# Revit family: CUSO
name_source: partatom
category: Lighting Fixtures
revit_build: Autodesk Revit 2014 (Build: 20130308_1515(x64)
units: mm (PartAtom-declared; Revit-internal decimal feet)

## types (1)
- CUSO
    Apparent Load = 32 VA
    Applications = The CUSO Series can be applied in areas that are susceptible
to rain and severe moisture like parking decks, and outdoor
commercial applications to meet all Path of Egress requirements.
    Color Filter = 16777215
    Colour Option = CUSO Series : Dark Bronze
    Compliances & Listings = UL924 Listed for Wet Location
NFPA 101 and NFPA 70
OSHA
    Default Elevation = 48 "
    Description = The CUSO Series is an architectural, low-profile outdoor light, offering normally on AC and emergency lighting with powerful LED illumination.
    Dimming Lamp Color Temperature Shift = <None>
    Features = Includes self-diagnostic/self-test feature to monitor
proper operation
•	 Quick installation
•	 Universal 120-277VAC input, 60Hz.
•	 Includes long-life 7.2V Nickel Cadmium battery for UL
recognized 90 minute operation
•	 Full re-charge within 24 hours
•	 Provided with water-proof test switch and AC-On
indicator
•	 0°C to 50°C Standard Model, -25°C to 50°C with
optional heater
•	 UL924 and Wet Location Listed
    Lamp = LED Lamp
    Load Classification = Lighting
    Manufacturer = Compass Lighting
    Model = CUSO
    Photometric Link = https://www.hubbell.com
    Photometric Web File = CUSO AC 3000K.ies
    Power Factor = 1
    Product Documentation Link = https://hubbellcdn.com
    Product Page URL = https://www.hubbell.com
    Tilt Angle = 90.00°
    URL = https://www.hubbell.com
    Voltage = 120 V
    Warranty = 5 year full unit warranty
    Watt = 32 W
    Wattage Comments = 17-32 W

## geometry (parser evidence)
native form markers: Blend x20, Sweep x4
no freeform markers — native parametric forms only
